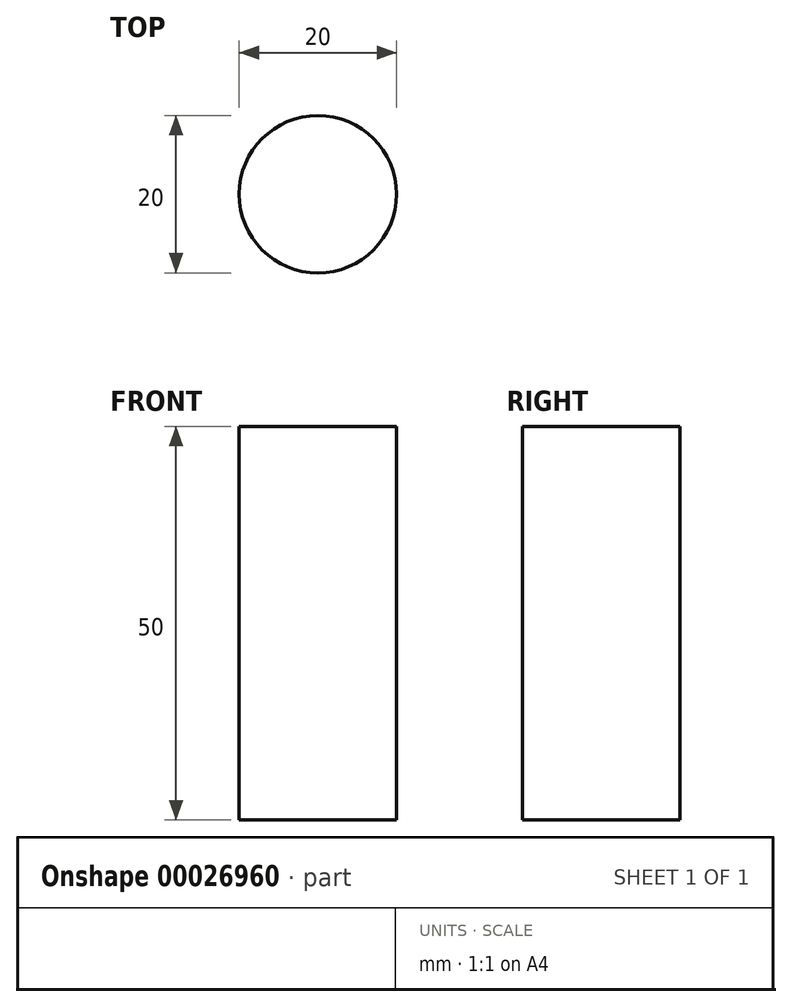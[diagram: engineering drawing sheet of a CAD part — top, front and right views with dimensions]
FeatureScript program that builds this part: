
annotation { "Feature Type Name" : "Feature", "Feature Type Description" : "" }
export const myFeature = defineFeature(function(context is Context, id is Id, definition is map)
    precondition{}
    {
        {
            var Q0;
            Q0=qCreatedBy(makeId("Top.planeOp"),FACE);
            var sketch = newSketch(context, id + "F0", { "sketchPlane" : qUnion([Q0])});
            skCircle(sketch, "E0", {"center": v(0, 0) * mm, "radius": 10 * mm});
            skSolve(sketch);
        }
        {
            var Q0;
            Q0 = qSketchRegion(id + "F0", true);
            extrude(context, id + "F1", {"entities" : qUnion([Q0]), "depth" : 50 * mm});
        }
    });
